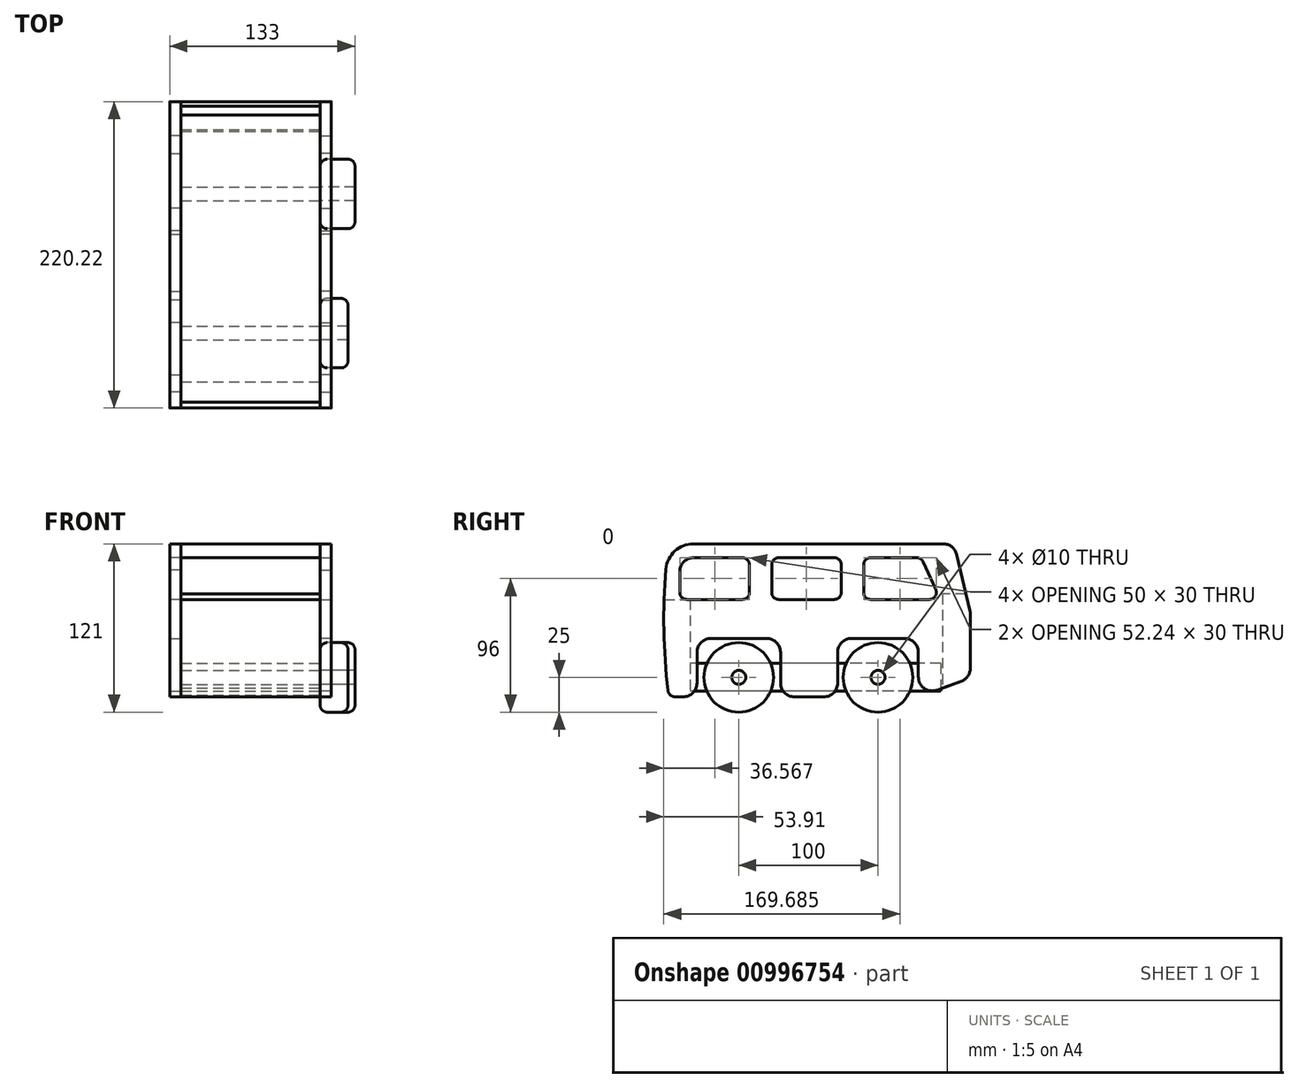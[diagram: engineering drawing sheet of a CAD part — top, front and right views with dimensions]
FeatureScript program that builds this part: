
annotation { "Feature Type Name" : "Feature", "Feature Type Description" : "" }
export const myFeature = defineFeature(function(context is Context, id is Id, definition is map)
    precondition{}
    {
        {
            var Q0;
            Q0=qCreatedBy(makeId("Top.planeOp"),FACE);
            var sketch = newSketch(context, id + "F0", { "sketchPlane" : qUnion([Q0])});
            skLineSegment(sketch, "E0.bottom", {"start": v(-50, 90) * mm, "end": v(50, 90) * mm});
            skLineSegment(sketch, "E0.top", {"start": v(-50, -90) * mm, "end": v(50, -90) * mm});
            skLineSegment(sketch, "E0.left", {"start": v(-50, 90) * mm, "end": v(-50, -90) * mm});
            skLineSegment(sketch, "E0.right", {"start": v(50, 90) * mm, "end": v(50, -90) * mm});
            skPoint(sketch, "E0.middle", {"position": v(0, 0) * mm});
            skSolve(sketch);
        }
        {
            var Q0;
            Q0 = qSketchRegion(id + "F0", true);
            extrude(context, id + "F1", {"entities" : qUnion([Q0]), "depth" : 10 * mm, "offsetDistance" : 25 * mm, "hasSecondDirection" : true, "secondDirectionOppositeDirection" : true, "secondDirectionDepth" : 10 * mm});
        }
        {
            var Q0;
            Q0=makeQuery(id+"F1.opExtrude","SWEPT_FACE",FACE,{"disambiguationData":[OSD([sQuery(id+"F0.wireOp",EDGE,"E0.right")])]});
            var sketch = newSketch(context, id + "F2", { "sketchPlane" : qUnion([Q0])});
            skCircle(sketch, "E1", {"center": v(-55, 0) * mm, "radius": 5 * mm});
            skCircle(sketch, "E2", {"center": v(45, 0) * mm, "radius": 5 * mm});
            skSolve(sketch);
        }
        {
            var Q0;
            Q0 = qSketchRegion(id + "F2", true);
            extrude(context, id + "F3", {"entities" : qUnion([Q0]), "operationType" : NewBodyOperationType.REMOVE, "endBound" : BoundingType.THROUGH_ALL, "oppositeDirection" : true, "depth" : 25 * mm, "offsetDistance" : 25 * mm});
        }
        {
            var Q0;
            {var subQ4=sQuery(id+"F0.wireOp",EDGE,"E0.right");Q0=makeQuery(id+"F11.boolean.opBoolean","SPLIT",FACE,{"disambiguationData":[TD([makeQuery(id+"F3.boolean.opBoolean","COPY",FACE,{"derivedFrom":makeQuery(id+"F3.opExtrude","SWEPT_FACE",FACE,{"disambiguationData":[OSD([sQuery(id+"F2.wireOp",EDGE,"E1")])]})})])],"derivedFrom":makeQuery(id+"F1.opExtrude","SWEPT_FACE",FACE,{"disambiguationData":[OSD([subQ4])]})});}
            var sketch = newSketch(context, id + "F4", { "sketchPlane" : qUnion([Q0])});
            skCircle(sketch, "E3.0", {"center": v(-55, 0) * mm, "radius": 5 * mm});
            skCircle(sketch, "E4", {"center": v(-55, 0) * mm, "radius": 25 * mm});
            skSolve(sketch);
        }
        {
            var Q0;
            Q0 = qSketchRegion(id + "F4", true);
            extrude(context, id + "F5", {"entities" : qUnion([Q0]), "depth" : 20 * mm, "offsetDistance" : 25 * mm});
        }
        {
            var Q0;
            Q0=makeQuery(id+"F5.opExtrude","SWEPT_FACE",FACE,{"disambiguationData":[OSD([sQuery(id+"F4.wireOp",EDGE,"E4")])]});
            fillet(context, id + "F6", {"entities" : qUnion([Q0]), "radius" : 5 * mm, "tangentPropagation" : true, "allowEdgeOverflow" : false});
        }
        {
            var Q0;
            Q0=makeQuery(id+"F1.opExtrude","SWEPT_FACE",FACE,{"disambiguationData":[OSD([sQuery(id+"F0.wireOp",EDGE,"E0.right")])]});
            var sketch = newSketch(context, id + "F7", { "sketchPlane" : qUnion([Q0])});
            skCircle(sketch, "E5.0", {"center": v(45, 0) * mm, "radius": 5 * mm});
            skCircle(sketch, "E6", {"center": v(45, 0) * mm, "radius": 25 * mm});
            skSolve(sketch);
        }
        {
            var Q0;
            Q0 = qSketchRegion(id + "F7", true);
            extrude(context, id + "F8", {"entities" : qUnion([Q0]), "depth" : 25 * mm, "offsetDistance" : 25 * mm});
        }
        {
            var Q0;
            Q0=makeQuery(id+"F8.opExtrude","SWEPT_FACE",FACE,{"disambiguationData":[OSD([sQuery(id+"F7.wireOp",EDGE,"E6")])]});
            fillet(context, id + "F9", {"entities" : qUnion([Q0]), "radius" : 5 * mm, "tangentPropagation" : true, "allowEdgeOverflow" : false});
        }
        {
            var Q0;
            Q0=makeQuery(id+"F1.opExtrude","SWEPT_FACE",FACE,{"disambiguationData":[OSD([sQuery(id+"F0.wireOp",EDGE,"E0.right")])]});
            var sketch = newSketch(context, id + "F10", { "sketchPlane" : qUnion([Q0])});
            skLineSegment(sketch, "E7", {"start": v(-87.42, 96) * mm, "end": v(91.8, 96) * mm});
            skLineSegment(sketch, "E8", {"start": v(101.53, 88.3) * mm, "end": v(111.04, 47.93) * mm});
            skLineSegment(sketch, "E9", {"start": v(111.3, 45.63) * mm, "end": v(111.3, 6.58) * mm});
            skLineSegment(sketch, "E10", {"start": v(104.73, -2.82) * mm, "end": v(87.42, -9.12) * mm});
            skLineSegment(sketch, "E11", {"start": v(74, 0.28) * mm, "end": v(74, 18) * mm});
            skLineSegment(sketch, "E12", {"start": v(64, 28) * mm, "end": v(26, 28) * mm});
            skLineSegment(sketch, "E13", {"start": v(16, 18) * mm, "end": v(16, -4) * mm});
            skLineSegment(sketch, "E14", {"start": v(6, -14) * mm, "end": v(-15, -14) * mm});
            skLineSegment(sketch, "E15", {"start": v(-25, -4) * mm, "end": v(-25, 18) * mm});
            skLineSegment(sketch, "E16", {"start": v(-35, 28) * mm, "end": v(-75, 28) * mm});
            skLineSegment(sketch, "E17", {"start": v(-85, 18) * mm, "end": v(-85, -4) * mm});
            skLineSegment(sketch, "E18", {"start": v(-95, -14) * mm, "end": v(-100.8, -14) * mm});
            skPoint(sketch, "E19.visualSharp", {"position": v(-94, 96) * mm});
            skArc(sketch, "E19.filletArc", {"start": v(-87.42, 96) * mm, "mid": v(-100.93, 90.74) * mm, "end": v(-107.34, 77.73) * mm});
            skPoint(sketch, "E20.visualSharp", {"position": v(-85, 28) * mm});
            skArc(sketch, "E20.filletArc", {"start": v(-75, 28) * mm, "mid": v(-82.07, 25.07) * mm, "end": v(-85, 18) * mm});
            skPoint(sketch, "E21.visualSharp", {"position": v(-25, 28) * mm});
            skArc(sketch, "E21.filletArc", {"start": v(-25, 18) * mm, "mid": v(-27.93, 25.07) * mm, "end": v(-35, 28) * mm});
            skPoint(sketch, "E22.visualSharp", {"position": v(16, 28) * mm});
            skArc(sketch, "E22.filletArc", {"start": v(26, 28) * mm, "mid": v(18.93, 25.07) * mm, "end": v(16, 18) * mm});
            skPoint(sketch, "E23.visualSharp", {"position": v(74, 28) * mm});
            skArc(sketch, "E23.filletArc", {"start": v(74, 18) * mm, "mid": v(71.07, 25.07) * mm, "end": v(64, 28) * mm});
            skArc(sketch, "E24.filletArc", {"start": v(-95, -14) * mm, "mid": v(-87.93, -11.07) * mm, "end": v(-85, -4) * mm});
            skPoint(sketch, "E25.visualSharp", {"position": v(-25, -14) * mm});
            skArc(sketch, "E25.filletArc", {"start": v(-25, -4) * mm, "mid": v(-22.07, -11.07) * mm, "end": v(-15, -14) * mm});
            skPoint(sketch, "E26.visualSharp", {"position": v(16, -14) * mm});
            skArc(sketch, "E26.filletArc", {"start": v(6, -14) * mm, "mid": v(13.07, -11.07) * mm, "end": v(16, -4) * mm});
            skPoint(sketch, "E27.visualSharp", {"position": v(74, -14) * mm});
            skArc(sketch, "E27.filletArc", {"start": v(74, 0.28) * mm, "mid": v(78.26, -7.91) * mm, "end": v(87.42, -9.12) * mm});
            skPoint(sketch, "E28.visualSharp", {"position": v(99.7, 96) * mm});
            skArc(sketch, "E28.filletArc", {"start": v(101.53, 88.3) * mm, "mid": v(98, 93.84) * mm, "end": v(91.8, 96) * mm});
            skPoint(sketch, "E29.visualSharp", {"position": v(111.3, 46.8) * mm});
            skArc(sketch, "E29.filletArc", {"start": v(111.3, 45.63) * mm, "mid": v(111.24, 46.79) * mm, "end": v(111.04, 47.93) * mm});
            skArc(sketch, "E30", {"start": v(-107.34, 77.73) * mm, "mid": v(-108.84, 34.02) * mm, "end": v(-105.76, -9.61) * mm});
            skPoint(sketch, "E31.visualSharp", {"position": v(-105.2, -14) * mm});
            skArc(sketch, "E31.filletArc", {"start": v(-105.76, -9.61) * mm, "mid": v(-104.11, -12.75) * mm, "end": v(-100.8, -14) * mm});
            skPoint(sketch, "E32.visualSharp", {"position": v(111.3, -0.42) * mm});
            skArc(sketch, "E32.filletArc", {"start": v(104.73, -2.82) * mm, "mid": v(109.5, 0.85) * mm, "end": v(111.3, 6.58) * mm});
            skSolve(sketch);
        }
        {
            var Q0;
            Q0 = qSketchRegion(id + "F10", true);
            extrude(context, id + "F11", {"entities" : qUnion([Q0]), "depth" : 8 * mm, "offsetDistance" : 25 * mm});
        }
        {
            var Q0;
            Q0=makeQuery(id+"F11.opExtrude","CAP_FACE",FACE,{"disambiguationData":[OSD([sQuery(id+"F10.wireOp",EDGE,"E7"),sQuery(id+"F10.wireOp",EDGE,"E8"),sQuery(id+"F10.wireOp",EDGE,"E9"),sQuery(id+"F10.wireOp",EDGE,"E10"),sQuery(id+"F10.wireOp",EDGE,"E11"),sQuery(id+"F10.wireOp",EDGE,"E12"),sQuery(id+"F10.wireOp",EDGE,"E13"),sQuery(id+"F10.wireOp",EDGE,"E14"),sQuery(id+"F10.wireOp",EDGE,"E15"),sQuery(id+"F10.wireOp",EDGE,"E16"),sQuery(id+"F10.wireOp",EDGE,"E17"),sQuery(id+"F10.wireOp",EDGE,"E18"),sQuery(id+"F10.wireOp",EDGE,"E19.filletArc"),sQuery(id+"F10.wireOp",EDGE,"E20.filletArc"),sQuery(id+"F10.wireOp",EDGE,"E21.filletArc"),sQuery(id+"F10.wireOp",EDGE,"E22.filletArc"),sQuery(id+"F10.wireOp",EDGE,"E23.filletArc"),sQuery(id+"F10.wireOp",EDGE,"E24.filletArc"),sQuery(id+"F10.wireOp",EDGE,"E25.filletArc"),sQuery(id+"F10.wireOp",EDGE,"E26.filletArc"),sQuery(id+"F10.wireOp",EDGE,"E27.filletArc"),sQuery(id+"F10.wireOp",EDGE,"E28.filletArc"),sQuery(id+"F10.wireOp",EDGE,"E29.filletArc"),sQuery(id+"F10.wireOp",EDGE,"E30"),sQuery(id+"F10.wireOp",EDGE,"E31.filletArc"),sQuery(id+"F10.wireOp",EDGE,"E32.filletArc")])],"isStart":false});
            var sketch = newSketch(context, id + "F12", { "sketchPlane" : qUnion([Q0])});
            skArc(sketch, "E33.0", {"start": v(-87.42, 86) * mm, "mid": v(-94.05, 83.49) * mm, "end": v(-97.34, 77.2) * mm});
            skLineSegment(sketch, "E33.1", {"start": v(-87.42, 86) * mm, "end": v(-52.34, 86) * mm});
            skLineSegment(sketch, "E33.2", {"start": v(91.8, 86) * mm, "end": v(91.8, 86) * mm});
            skLineSegment(sketch, "E34", {"start": v(-97.34, 77.2) * mm, "end": v(-97.34, 61) * mm});
            skLineSegment(sketch, "E35", {"start": v(-92.34, 56) * mm, "end": v(-52.34, 56) * mm});
            skLineSegment(sketch, "E36", {"start": v(-47.34, 61) * mm, "end": v(-47.34, 81) * mm});
            skLineSegment(sketch, "E37", {"start": v(-31.34, 81) * mm, "end": v(-31.34, 61) * mm});
            skLineSegment(sketch, "E38", {"start": v(-26.34, 56) * mm, "end": v(13.66, 56) * mm});
            skLineSegment(sketch, "E39", {"start": v(18.66, 61) * mm, "end": v(18.66, 81) * mm});
            skLineSegment(sketch, "E40", {"start": v(77.43, 83.06) * mm, "end": v(86.46, 63.06) * mm});
            skLineSegment(sketch, "E41", {"start": v(81.9, 56) * mm, "end": v(39.66, 56) * mm});
            skLineSegment(sketch, "E42", {"start": v(34.66, 61) * mm, "end": v(34.66, 81) * mm});
            skLineSegment(sketch, "E43.trimOffspring", {"start": v(-26.34, 86) * mm, "end": v(13.66, 86) * mm});
            skLineSegment(sketch, "E44.trimOffspring", {"start": v(39.66, 86) * mm, "end": v(72.88, 86) * mm});
            skPoint(sketch, "E45.visualSharp", {"position": v(-47.34, 86) * mm});
            skArc(sketch, "E45.filletArc", {"start": v(-47.34, 81) * mm, "mid": v(-48.8, 84.54) * mm, "end": v(-52.34, 86) * mm});
            skPoint(sketch, "E46.visualSharp", {"position": v(-31.34, 86) * mm});
            skArc(sketch, "E46.filletArc", {"start": v(-26.34, 86) * mm, "mid": v(-29.88, 84.54) * mm, "end": v(-31.34, 81) * mm});
            skPoint(sketch, "E47.visualSharp", {"position": v(18.66, 86) * mm});
            skArc(sketch, "E47.filletArc", {"start": v(18.66, 81) * mm, "mid": v(17.2, 84.54) * mm, "end": v(13.66, 86) * mm});
            skPoint(sketch, "E48.visualSharp", {"position": v(34.66, 86) * mm});
            skArc(sketch, "E48.filletArc", {"start": v(39.66, 86) * mm, "mid": v(36.12, 84.54) * mm, "end": v(34.66, 81) * mm});
            skPoint(sketch, "E49.visualSharp", {"position": v(76.1, 86) * mm});
            skArc(sketch, "E49.filletArc", {"start": v(77.43, 83.06) * mm, "mid": v(75.59, 85.2) * mm, "end": v(72.88, 86) * mm});
            skPoint(sketch, "E50.visualSharp", {"position": v(89.65, 56) * mm});
            skArc(sketch, "E50.filletArc", {"start": v(81.9, 56) * mm, "mid": v(86.1, 58.29) * mm, "end": v(86.46, 63.06) * mm});
            skPoint(sketch, "E51.visualSharp", {"position": v(34.66, 56) * mm});
            skArc(sketch, "E51.filletArc", {"start": v(34.66, 61) * mm, "mid": v(36.12, 57.46) * mm, "end": v(39.66, 56) * mm});
            skPoint(sketch, "E52.visualSharp", {"position": v(18.66, 56) * mm});
            skArc(sketch, "E52.filletArc", {"start": v(13.66, 56) * mm, "mid": v(17.2, 57.46) * mm, "end": v(18.66, 61) * mm});
            skPoint(sketch, "E53.visualSharp", {"position": v(-31.34, 56) * mm});
            skArc(sketch, "E53.filletArc", {"start": v(-31.34, 61) * mm, "mid": v(-29.88, 57.46) * mm, "end": v(-26.34, 56) * mm});
            skPoint(sketch, "E54.visualSharp", {"position": v(-47.34, 56) * mm});
            skArc(sketch, "E54.filletArc", {"start": v(-52.34, 56) * mm, "mid": v(-48.8, 57.46) * mm, "end": v(-47.34, 61) * mm});
            skPoint(sketch, "E55.visualSharp", {"position": v(-97.34, 56) * mm});
            skArc(sketch, "E55.filletArc", {"start": v(-97.34, 61) * mm, "mid": v(-95.88, 57.46) * mm, "end": v(-92.34, 56) * mm});
            skSolve(sketch);
        }
        {
            var Q0;
            Q0 = qSketchRegion(id + "F12", true);
            extrude(context, id + "F13", {"entities" : qUnion([Q0]), "operationType" : NewBodyOperationType.REMOVE, "endBound" : BoundingType.THROUGH_ALL, "oppositeDirection" : true, "depth" : 25 * mm, "offsetDistance" : 25 * mm});
        }
        {
            var Q0;
            Q0=makeQuery(id+"F11.opExtrude","SWEPT_BODY",BODY,{"disambiguationData":[OSD([sQuery(id+"F10.wireOp",EDGE,"E7"),sQuery(id+"F10.wireOp",EDGE,"E8"),sQuery(id+"F10.wireOp",EDGE,"E9"),sQuery(id+"F10.wireOp",EDGE,"E10"),sQuery(id+"F10.wireOp",EDGE,"E11"),sQuery(id+"F10.wireOp",EDGE,"E12"),sQuery(id+"F10.wireOp",EDGE,"E13"),sQuery(id+"F10.wireOp",EDGE,"E14"),sQuery(id+"F10.wireOp",EDGE,"E15"),sQuery(id+"F10.wireOp",EDGE,"E16"),sQuery(id+"F10.wireOp",EDGE,"E17"),sQuery(id+"F10.wireOp",EDGE,"E18"),sQuery(id+"F10.wireOp",EDGE,"E19.filletArc"),sQuery(id+"F10.wireOp",EDGE,"E20.filletArc"),sQuery(id+"F10.wireOp",EDGE,"E21.filletArc"),sQuery(id+"F10.wireOp",EDGE,"E22.filletArc"),sQuery(id+"F10.wireOp",EDGE,"E23.filletArc"),sQuery(id+"F10.wireOp",EDGE,"E24.filletArc"),sQuery(id+"F10.wireOp",EDGE,"E25.filletArc"),sQuery(id+"F10.wireOp",EDGE,"E26.filletArc"),sQuery(id+"F10.wireOp",EDGE,"E27.filletArc"),sQuery(id+"F10.wireOp",EDGE,"E28.filletArc"),sQuery(id+"F10.wireOp",EDGE,"E29.filletArc"),sQuery(id+"F10.wireOp",EDGE,"E30"),sQuery(id+"F10.wireOp",EDGE,"E31.filletArc"),sQuery(id+"F10.wireOp",EDGE,"E32.filletArc")])]});
            var Q1;
            Q1=qCreatedBy(makeId("Right.planeOp"),FACE);
            mirror(context, id + "F14", {"entities" : qUnion([Q0]), "mirrorPlane" : qUnion([Q1])});
        }
        {
            var Q0;
            Q0=makeQuery(id+"F11.opExtrude","CAP_FACE",FACE,{"disambiguationData":[OSD([sQuery(id+"F10.wireOp",EDGE,"E7"),sQuery(id+"F10.wireOp",EDGE,"E8"),sQuery(id+"F10.wireOp",EDGE,"E9"),sQuery(id+"F10.wireOp",EDGE,"E10"),sQuery(id+"F10.wireOp",EDGE,"E11"),sQuery(id+"F10.wireOp",EDGE,"E12"),sQuery(id+"F10.wireOp",EDGE,"E13"),sQuery(id+"F10.wireOp",EDGE,"E14"),sQuery(id+"F10.wireOp",EDGE,"E15"),sQuery(id+"F10.wireOp",EDGE,"E16"),sQuery(id+"F10.wireOp",EDGE,"E17"),sQuery(id+"F10.wireOp",EDGE,"E18"),sQuery(id+"F10.wireOp",EDGE,"E19.filletArc"),sQuery(id+"F10.wireOp",EDGE,"E20.filletArc"),sQuery(id+"F10.wireOp",EDGE,"E21.filletArc"),sQuery(id+"F10.wireOp",EDGE,"E22.filletArc"),sQuery(id+"F10.wireOp",EDGE,"E23.filletArc"),sQuery(id+"F10.wireOp",EDGE,"E24.filletArc"),sQuery(id+"F10.wireOp",EDGE,"E25.filletArc"),sQuery(id+"F10.wireOp",EDGE,"E26.filletArc"),sQuery(id+"F10.wireOp",EDGE,"E27.filletArc"),sQuery(id+"F10.wireOp",EDGE,"E28.filletArc"),sQuery(id+"F10.wireOp",EDGE,"E29.filletArc"),sQuery(id+"F10.wireOp",EDGE,"E30"),sQuery(id+"F10.wireOp",EDGE,"E31.filletArc"),sQuery(id+"F10.wireOp",EDGE,"E32.filletArc")])],"isStart":true});
            var sketch = newSketch(context, id + "F15", { "sketchPlane" : qUnion([Q0])});
            skArc(sketch, "E56.0", {"start": v(-101.8, 86) * mm, "mid": v(-98.86, 93.07) * mm, "end": v(-91.8, 96) * mm});
            skLineSegment(sketch, "E56.1", {"start": v(87.42, 96) * mm, "end": v(-91.8, 96) * mm});
            skArc(sketch, "E56.2", {"start": v(87.42, 96) * mm, "mid": v(97.42, 93.32) * mm, "end": v(104.74, 86) * mm});
            skLineSegment(sketch, "E57.0", {"start": v(104.74, 86) * mm, "end": v(-101.8, 86) * mm});
            skPoint(sketch, "E58.orphan", {"position": v(-101.53, 88.3) * mm});
            skPoint(sketch, "E59.orphan", {"position": v(107.34, 77.73) * mm});
            skSolve(sketch);
        }
        {
            var Q0;
            Q0 = qSketchRegion(id + "F15", true);
            var Q1;
            Q1=makeQuery(id+"F14.opPattern","COPY",FACE,{"derivedFrom":makeQuery(id+"F11.opExtrude","CAP_FACE",FACE,{"disambiguationData":[OSD([sQuery(id+"F10.wireOp",EDGE,"E7"),sQuery(id+"F10.wireOp",EDGE,"E8"),sQuery(id+"F10.wireOp",EDGE,"E9"),sQuery(id+"F10.wireOp",EDGE,"E10"),sQuery(id+"F10.wireOp",EDGE,"E11"),sQuery(id+"F10.wireOp",EDGE,"E12"),sQuery(id+"F10.wireOp",EDGE,"E13"),sQuery(id+"F10.wireOp",EDGE,"E14"),sQuery(id+"F10.wireOp",EDGE,"E15"),sQuery(id+"F10.wireOp",EDGE,"E16"),sQuery(id+"F10.wireOp",EDGE,"E17"),sQuery(id+"F10.wireOp",EDGE,"E18"),sQuery(id+"F10.wireOp",EDGE,"E19.filletArc"),sQuery(id+"F10.wireOp",EDGE,"E20.filletArc"),sQuery(id+"F10.wireOp",EDGE,"E21.filletArc"),sQuery(id+"F10.wireOp",EDGE,"E22.filletArc"),sQuery(id+"F10.wireOp",EDGE,"E23.filletArc"),sQuery(id+"F10.wireOp",EDGE,"E24.filletArc"),sQuery(id+"F10.wireOp",EDGE,"E25.filletArc"),sQuery(id+"F10.wireOp",EDGE,"E26.filletArc"),sQuery(id+"F10.wireOp",EDGE,"E27.filletArc"),sQuery(id+"F10.wireOp",EDGE,"E28.filletArc"),sQuery(id+"F10.wireOp",EDGE,"E29.filletArc"),sQuery(id+"F10.wireOp",EDGE,"E30"),sQuery(id+"F10.wireOp",EDGE,"E31.filletArc"),sQuery(id+"F10.wireOp",EDGE,"E32.filletArc")])],"isStart":true}),"instanceName":"1"});
            extrude(context, id + "F16", {"entities" : qUnion([Q0]), "endBound" : BoundingType.UP_TO_SURFACE, "depth" : 25 * mm, "endBoundEntityFace" : qUnion([Q1]), "offsetDistance" : 25 * mm});
        }
        {
            var Q0;
            Q0=makeQuery(id+"F11.opExtrude","CAP_FACE",FACE,{"disambiguationData":[OSD([sQuery(id+"F10.wireOp",EDGE,"E7"),sQuery(id+"F10.wireOp",EDGE,"E8"),sQuery(id+"F10.wireOp",EDGE,"E9"),sQuery(id+"F10.wireOp",EDGE,"E10"),sQuery(id+"F10.wireOp",EDGE,"E11"),sQuery(id+"F10.wireOp",EDGE,"E12"),sQuery(id+"F10.wireOp",EDGE,"E13"),sQuery(id+"F10.wireOp",EDGE,"E14"),sQuery(id+"F10.wireOp",EDGE,"E15"),sQuery(id+"F10.wireOp",EDGE,"E16"),sQuery(id+"F10.wireOp",EDGE,"E17"),sQuery(id+"F10.wireOp",EDGE,"E18"),sQuery(id+"F10.wireOp",EDGE,"E19.filletArc"),sQuery(id+"F10.wireOp",EDGE,"E20.filletArc"),sQuery(id+"F10.wireOp",EDGE,"E21.filletArc"),sQuery(id+"F10.wireOp",EDGE,"E22.filletArc"),sQuery(id+"F10.wireOp",EDGE,"E23.filletArc"),sQuery(id+"F10.wireOp",EDGE,"E24.filletArc"),sQuery(id+"F10.wireOp",EDGE,"E25.filletArc"),sQuery(id+"F10.wireOp",EDGE,"E26.filletArc"),sQuery(id+"F10.wireOp",EDGE,"E27.filletArc"),sQuery(id+"F10.wireOp",EDGE,"E28.filletArc"),sQuery(id+"F10.wireOp",EDGE,"E29.filletArc"),sQuery(id+"F10.wireOp",EDGE,"E30"),sQuery(id+"F10.wireOp",EDGE,"E31.filletArc"),sQuery(id+"F10.wireOp",EDGE,"E32.filletArc")])],"isStart":true});
            var sketch = newSketch(context, id + "F17", { "sketchPlane" : qUnion([Q0])});
            skLineSegment(sketch, "E60.0", {"start": v(-104.73, -2.82) * mm, "end": v(-91.3, -7.7) * mm});
            skArc(sketch, "E60.1", {"start": v(-104.73, -2.82) * mm, "mid": v(-109.5, 0.85) * mm, "end": v(-111.3, 6.58) * mm});
            skLineSegment(sketch, "E60.2", {"start": v(-111.3, 45.63) * mm, "end": v(-111.3, 6.58) * mm});
            skArc(sketch, "E60.3", {"start": v(-111.3, 45.63) * mm, "mid": v(-111.24, 46.79) * mm, "end": v(-111.04, 47.93) * mm});
            skLineSegment(sketch, "E60.4", {"start": v(-108.2, 60) * mm, "end": v(-111.04, 47.93) * mm});
            skLineSegment(sketch, "E61", {"start": v(-108.2, 60) * mm, "end": v(-91.3, 60) * mm});
            skLineSegment(sketch, "E62.3", {"start": v(-91.3, 60) * mm, "end": v(-91.3, -7.7) * mm});
            skPoint(sketch, "E63.orphan", {"position": v(-87.42, -9.12) * mm});
            skPoint(sketch, "E64.orphan", {"position": v(-101.53, 88.3) * mm});
            skSolve(sketch);
        }
        {
            var Q0;
            Q0 = qSketchRegion(id + "F17", true);
            var Q1;
            Q1=makeQuery(id+"F14.opPattern","COPY",FACE,{"derivedFrom":makeQuery(id+"F11.opExtrude","CAP_FACE",FACE,{"disambiguationData":[OSD([sQuery(id+"F10.wireOp",EDGE,"E7"),sQuery(id+"F10.wireOp",EDGE,"E8"),sQuery(id+"F10.wireOp",EDGE,"E9"),sQuery(id+"F10.wireOp",EDGE,"E10"),sQuery(id+"F10.wireOp",EDGE,"E11"),sQuery(id+"F10.wireOp",EDGE,"E12"),sQuery(id+"F10.wireOp",EDGE,"E13"),sQuery(id+"F10.wireOp",EDGE,"E14"),sQuery(id+"F10.wireOp",EDGE,"E15"),sQuery(id+"F10.wireOp",EDGE,"E16"),sQuery(id+"F10.wireOp",EDGE,"E17"),sQuery(id+"F10.wireOp",EDGE,"E18"),sQuery(id+"F10.wireOp",EDGE,"E19.filletArc"),sQuery(id+"F10.wireOp",EDGE,"E20.filletArc"),sQuery(id+"F10.wireOp",EDGE,"E21.filletArc"),sQuery(id+"F10.wireOp",EDGE,"E22.filletArc"),sQuery(id+"F10.wireOp",EDGE,"E23.filletArc"),sQuery(id+"F10.wireOp",EDGE,"E24.filletArc"),sQuery(id+"F10.wireOp",EDGE,"E25.filletArc"),sQuery(id+"F10.wireOp",EDGE,"E26.filletArc"),sQuery(id+"F10.wireOp",EDGE,"E27.filletArc"),sQuery(id+"F10.wireOp",EDGE,"E28.filletArc"),sQuery(id+"F10.wireOp",EDGE,"E29.filletArc"),sQuery(id+"F10.wireOp",EDGE,"E30"),sQuery(id+"F10.wireOp",EDGE,"E31.filletArc"),sQuery(id+"F10.wireOp",EDGE,"E32.filletArc")])],"isStart":true}),"instanceName":"1"});
            extrude(context, id + "F18", {"entities" : qUnion([Q0]), "endBound" : BoundingType.UP_TO_SURFACE, "depth" : 25 * mm, "endBoundEntityFace" : qUnion([Q1]), "offsetDistance" : 25 * mm});
        }
        {
            var Q0;
            Q0=makeQuery(id+"F11.opExtrude","CAP_FACE",FACE,{"disambiguationData":[OSD([sQuery(id+"F10.wireOp",EDGE,"E7"),sQuery(id+"F10.wireOp",EDGE,"E8"),sQuery(id+"F10.wireOp",EDGE,"E9"),sQuery(id+"F10.wireOp",EDGE,"E10"),sQuery(id+"F10.wireOp",EDGE,"E11"),sQuery(id+"F10.wireOp",EDGE,"E12"),sQuery(id+"F10.wireOp",EDGE,"E13"),sQuery(id+"F10.wireOp",EDGE,"E14"),sQuery(id+"F10.wireOp",EDGE,"E15"),sQuery(id+"F10.wireOp",EDGE,"E16"),sQuery(id+"F10.wireOp",EDGE,"E17"),sQuery(id+"F10.wireOp",EDGE,"E18"),sQuery(id+"F10.wireOp",EDGE,"E19.filletArc"),sQuery(id+"F10.wireOp",EDGE,"E20.filletArc"),sQuery(id+"F10.wireOp",EDGE,"E21.filletArc"),sQuery(id+"F10.wireOp",EDGE,"E22.filletArc"),sQuery(id+"F10.wireOp",EDGE,"E23.filletArc"),sQuery(id+"F10.wireOp",EDGE,"E24.filletArc"),sQuery(id+"F10.wireOp",EDGE,"E25.filletArc"),sQuery(id+"F10.wireOp",EDGE,"E26.filletArc"),sQuery(id+"F10.wireOp",EDGE,"E27.filletArc"),sQuery(id+"F10.wireOp",EDGE,"E28.filletArc"),sQuery(id+"F10.wireOp",EDGE,"E29.filletArc"),sQuery(id+"F10.wireOp",EDGE,"E30"),sQuery(id+"F10.wireOp",EDGE,"E31.filletArc"),sQuery(id+"F10.wireOp",EDGE,"E32.filletArc")])],"isStart":true});
            var sketch = newSketch(context, id + "F19", { "sketchPlane" : qUnion([Q0])});
            skArc(sketch, "E65.1", {"start": v(108.66, 56) * mm, "mid": v(108.5, 23.14) * mm, "end": v(105.76, -9.61) * mm});
            skArc(sketch, "E65.2", {"start": v(105.76, -9.61) * mm, "mid": v(104.11, -12.75) * mm, "end": v(100.8, -14) * mm});
            skLineSegment(sketch, "E65.3", {"start": v(95, -14) * mm, "end": v(100.8, -14) * mm});
            skPoint(sketch, "E66.endSnap0", {"position": v(85, 7) * mm});
            skLineSegment(sketch, "E67.0", {"start": v(90, 56) * mm, "end": v(90, -12.66) * mm});
            skPoint(sketch, "E68.orphan", {"position": v(90, 10) * mm});
            skPoint(sketch, "E69.orphan", {"position": v(90, -10) * mm});
            skArc(sketch, "E70.0", {"start": v(95, -14) * mm, "mid": v(92.41, -13.66) * mm, "end": v(90, -12.66) * mm});
            skPoint(sketch, "E71.orphan", {"position": v(85, -4) * mm});
            skLineSegment(sketch, "E72.0", {"start": v(108.66, 56) * mm, "end": v(90, 56) * mm});
            skPoint(sketch, "E73.orphan", {"position": v(92.34, 56) * mm});
            skPoint(sketch, "E74.orphan", {"position": v(52.34, 56) * mm});
            skPoint(sketch, "E75.orphan", {"position": v(107.34, 77.73) * mm});
            skSolve(sketch);
        }
        {
            var Q0;
            Q0 = qSketchRegion(id + "F19", true);
            var Q1;
            Q1=makeQuery(id+"F14.opPattern","COPY",FACE,{"derivedFrom":makeQuery(id+"F11.opExtrude","CAP_FACE",FACE,{"disambiguationData":[OSD([sQuery(id+"F10.wireOp",EDGE,"E7"),sQuery(id+"F10.wireOp",EDGE,"E8"),sQuery(id+"F10.wireOp",EDGE,"E9"),sQuery(id+"F10.wireOp",EDGE,"E10"),sQuery(id+"F10.wireOp",EDGE,"E11"),sQuery(id+"F10.wireOp",EDGE,"E12"),sQuery(id+"F10.wireOp",EDGE,"E13"),sQuery(id+"F10.wireOp",EDGE,"E14"),sQuery(id+"F10.wireOp",EDGE,"E15"),sQuery(id+"F10.wireOp",EDGE,"E16"),sQuery(id+"F10.wireOp",EDGE,"E17"),sQuery(id+"F10.wireOp",EDGE,"E18"),sQuery(id+"F10.wireOp",EDGE,"E19.filletArc"),sQuery(id+"F10.wireOp",EDGE,"E20.filletArc"),sQuery(id+"F10.wireOp",EDGE,"E21.filletArc"),sQuery(id+"F10.wireOp",EDGE,"E22.filletArc"),sQuery(id+"F10.wireOp",EDGE,"E23.filletArc"),sQuery(id+"F10.wireOp",EDGE,"E24.filletArc"),sQuery(id+"F10.wireOp",EDGE,"E25.filletArc"),sQuery(id+"F10.wireOp",EDGE,"E26.filletArc"),sQuery(id+"F10.wireOp",EDGE,"E27.filletArc"),sQuery(id+"F10.wireOp",EDGE,"E28.filletArc"),sQuery(id+"F10.wireOp",EDGE,"E29.filletArc"),sQuery(id+"F10.wireOp",EDGE,"E30"),sQuery(id+"F10.wireOp",EDGE,"E31.filletArc"),sQuery(id+"F10.wireOp",EDGE,"E32.filletArc")])],"isStart":true}),"instanceName":"1"});
            extrude(context, id + "F20", {"entities" : qUnion([Q0]), "endBound" : BoundingType.UP_TO_SURFACE, "depth" : 25 * mm, "endBoundEntityFace" : qUnion([Q1]), "offsetDistance" : 25 * mm});
        }
    });
